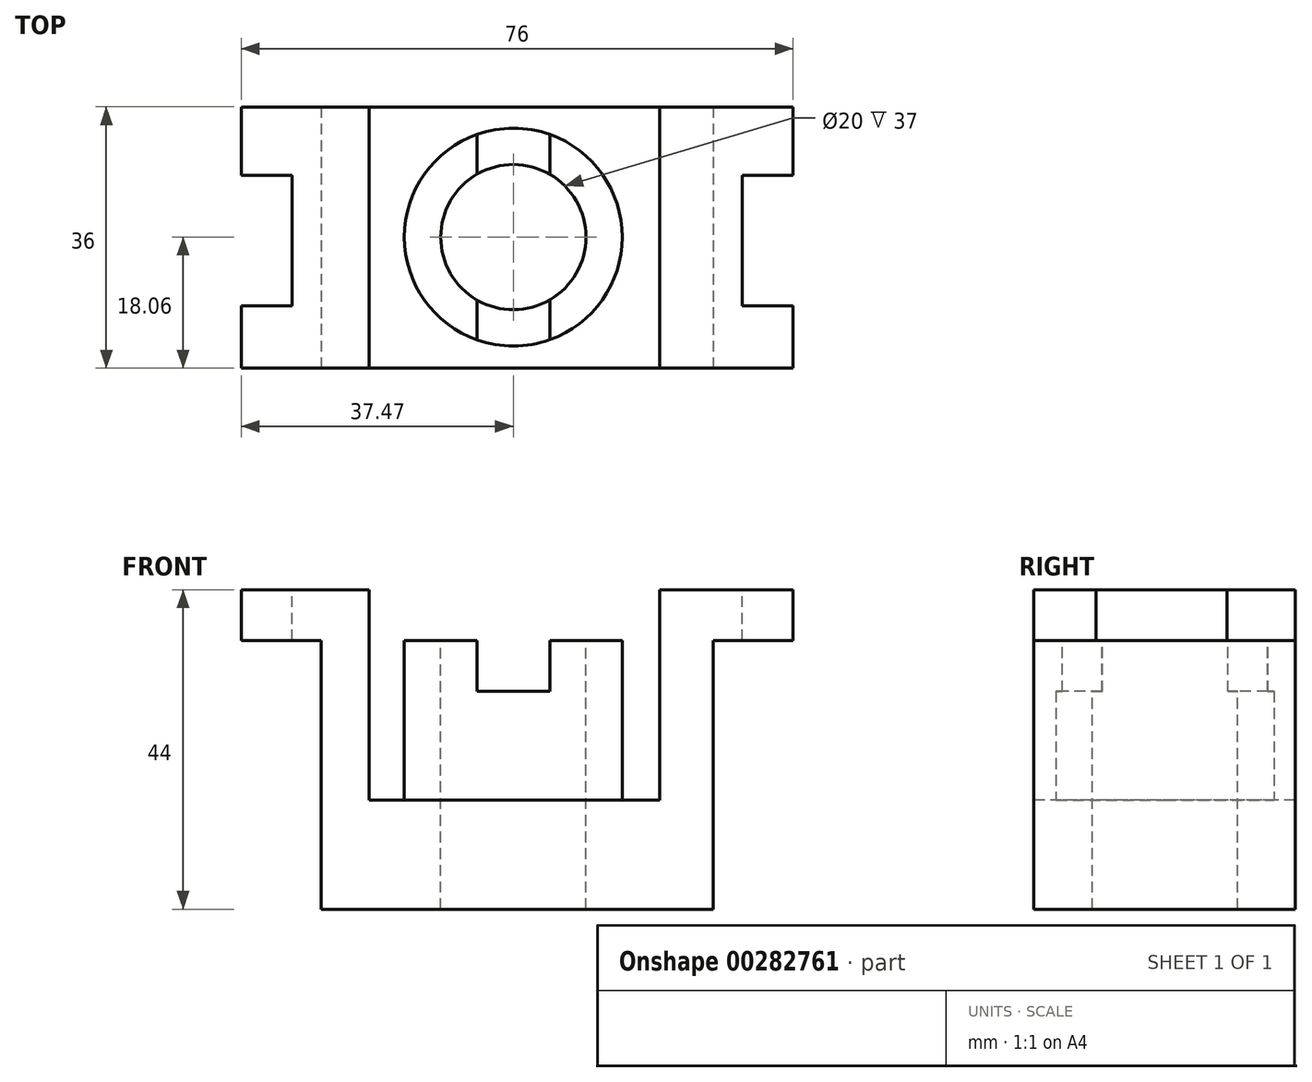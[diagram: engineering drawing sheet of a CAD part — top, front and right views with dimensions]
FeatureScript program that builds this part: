
annotation { "Feature Type Name" : "Feature", "Feature Type Description" : "" }
export const myFeature = defineFeature(function(context is Context, id is Id, definition is map)
    precondition{}
    {
        {
            var Q0;
            Q0=qCreatedBy(makeId("Top.planeOp"),FACE);
            var sketch = newSketch(context, id + "F0", { "sketchPlane" : qUnion([Q0])});
            skLineSegment(sketch, "E0.bottom", {"start": v(-14.48, -0.41) * mm, "end": v(39.52, -0.41) * mm});
            skLineSegment(sketch, "E0.top", {"start": v(-14.48, -36.41) * mm, "end": v(39.52, -36.41) * mm});
            skLineSegment(sketch, "E0.left", {"start": v(-14.48, -0.41) * mm, "end": v(-14.48, -36.41) * mm});
            skLineSegment(sketch, "E0.right", {"start": v(39.52, -0.41) * mm, "end": v(39.52, -36.41) * mm});
            skSolve(sketch);
        }
        {
            var Q0;
            Q0=makeQuery(id+"F0.imprint","IMPRINT",FACE,{"disambiguationData":[TD([[makeQuery(id+"F0.imprint","IMPRINT",EDGE,{"derivedFrom":sQuery(id+"F0.wireOp",EDGE,"E0.bottom")}),-1.0]])]});
            extrude(context, id + "F1", {"entities" : qUnion([Q0]), "depth" : 44 * mm});
        }
        {
            var Q0;
            Q0=makeQuery(id+"F1.opExtrude","SWEPT_FACE",FACE,{"disambiguationData":[OSD([sQuery(id+"F0.wireOp",EDGE,"E0.top")])]});
            var sketch = newSketch(context, id + "F2", { "sketchPlane" : qUnion([Q0])});
            skLineSegment(sketch, "E1.bottom", {"start": v(-7.85, 15) * mm, "end": v(32.15, 15) * mm});
            skLineSegment(sketch, "E1.top", {"start": v(-7.85, 44) * mm, "end": v(32.15, 44) * mm});
            skLineSegment(sketch, "E1.left", {"start": v(-7.85, 15) * mm, "end": v(-7.85, 44) * mm});
            skLineSegment(sketch, "E1.right", {"start": v(32.15, 15) * mm, "end": v(32.15, 44) * mm});
            skSolve(sketch);
        }
        {
            var Q0;
            Q0=makeQuery(id+"F2.imprint","IMPRINT",FACE,{"disambiguationData":[TD([[makeQuery(id+"F2.imprint","IMPRINT",EDGE,{"derivedFrom":sQuery(id+"F2.wireOp",EDGE,"E1.bottom")}),1.0]])]});
            extrude(context, id + "F3", {"entities" : qUnion([Q0]), "operationType" : NewBodyOperationType.REMOVE, "oppositeDirection" : true, "depth" : 36 * mm});
        }
        {
            var Q0;
            {var subQ0=sQuery(id+"F0.wireOp",EDGE,"E0.bottom");var subQ1=sQuery(id+"F0.wireOp",EDGE,"E0.right");var subQ2=sQuery(id+"F0.wireOp",EDGE,"E0.top");Q0=makeQuery(id+"F3.boolean.opBoolean","SPLIT",FACE,{"disambiguationData":[TD([makeQuery(id+"F1.opExtrude","SWEPT_FACE",FACE,{"disambiguationData":[OSD([subQ1])]})])],"derivedFrom":makeQuery(id+"F1.opExtrude","CAP_FACE",FACE,{"disambiguationData":[OSD([subQ0,subQ2,sQuery(id+"F0.wireOp",EDGE,"E0.left"),subQ1])],"isStart":false})});}
            var sketch = newSketch(context, id + "F4", { "sketchPlane" : qUnion([Q0])});
            skLineSegment(sketch, "E2.bottom", {"start": v(39.52, -0.41) * mm, "end": v(50.52, -0.41) * mm});
            skLineSegment(sketch, "E2.top", {"start": v(39.52, -36.41) * mm, "end": v(50.52, -36.41) * mm});
            skLineSegment(sketch, "E2.left", {"start": v(39.52, -0.41) * mm, "end": v(39.52, -36.41) * mm});
            skLineSegment(sketch, "E2.right", {"start": v(50.52, -0.41) * mm, "end": v(50.52, -36.41) * mm});
            skSolve(sketch);
        }
        {
            var Q0;
            Q0=makeQuery(id+"F4.imprint","IMPRINT",FACE,{"disambiguationData":[TD([[makeQuery(id+"F4.imprint","IMPRINT",EDGE,{"derivedFrom":sQuery(id+"F4.wireOp",EDGE,"E2.bottom")}),-1.0]])]});
            extrude(context, id + "F5", {"entities" : qUnion([Q0]), "operationType" : NewBodyOperationType.ADD, "oppositeDirection" : true, "depth" : 7 * mm});
        }
        {
            var Q0;
            {var subQ0=sQuery(id+"F0.wireOp",EDGE,"E0.bottom");var subQ1=sQuery(id+"F0.wireOp",EDGE,"E0.right");var subQ2=sQuery(id+"F0.wireOp",EDGE,"E0.top");Q0=makeQuery(id+"F5.boolean.opBoolean","MERGE",FACE,{"derivedFrom":[makeQuery(id+"F3.boolean.opBoolean","SPLIT",FACE,{"disambiguationData":[TD([makeQuery(id+"F1.opExtrude","SWEPT_FACE",FACE,{"disambiguationData":[OSD([subQ1])]})])],"derivedFrom":makeQuery(id+"F1.opExtrude","CAP_FACE",FACE,{"disambiguationData":[OSD([subQ0,subQ2,sQuery(id+"F0.wireOp",EDGE,"E0.left"),subQ1])],"isStart":false})}),makeQuery(id+"F5.opExtrude","CAP_FACE",FACE,{"disambiguationData":[OSD([sQuery(id+"F4.wireOp",EDGE,"E2.bottom"),sQuery(id+"F4.wireOp",EDGE,"E2.top"),sQuery(id+"F4.wireOp",EDGE,"E2.left"),sQuery(id+"F4.wireOp",EDGE,"E2.right")])],"isStart":true})]});}
            var sketch = newSketch(context, id + "F6", { "sketchPlane" : qUnion([Q0])});
            skLineSegment(sketch, "E3.bottom", {"start": v(43.52, -9.83) * mm, "end": v(50.52, -9.83) * mm});
            skLineSegment(sketch, "E3.top", {"start": v(43.52, -27.83) * mm, "end": v(50.52, -27.83) * mm});
            skLineSegment(sketch, "E3.left", {"start": v(43.52, -9.83) * mm, "end": v(43.52, -27.83) * mm});
            skLineSegment(sketch, "E3.right", {"start": v(50.52, -9.83) * mm, "end": v(50.52, -27.83) * mm});
            skSolve(sketch);
        }
        {
            var Q0;
            Q0=makeQuery(id+"F6.imprint","IMPRINT",FACE,{"disambiguationData":[TD([[makeQuery(id+"F6.imprint","IMPRINT",EDGE,{"derivedFrom":sQuery(id+"F6.wireOp",EDGE,"E3.bottom")}),-1.0]])]});
            extrude(context, id + "F7", {"entities" : qUnion([Q0]), "operationType" : NewBodyOperationType.REMOVE, "oppositeDirection" : true, "depth" : 7 * mm});
        }
        {
            var Q0;
            {var subQ0=sQuery(id+"F0.wireOp",EDGE,"E0.bottom");var subQ1=sQuery(id+"F0.wireOp",EDGE,"E0.top");var subQ2=sQuery(id+"F0.wireOp",EDGE,"E0.left");Q0=makeQuery(id+"F3.boolean.opBoolean","SPLIT",FACE,{"disambiguationData":[TD([makeQuery(id+"F1.opExtrude","SWEPT_FACE",FACE,{"disambiguationData":[OSD([subQ2])]})])],"derivedFrom":makeQuery(id+"F1.opExtrude","CAP_FACE",FACE,{"disambiguationData":[OSD([subQ0,subQ1,subQ2,sQuery(id+"F0.wireOp",EDGE,"E0.right")])],"isStart":false})});}
            var sketch = newSketch(context, id + "F8", { "sketchPlane" : qUnion([Q0])});
            skLineSegment(sketch, "E4.bottom", {"start": v(-25.48, -36.41) * mm, "end": v(-14.48, -36.41) * mm});
            skLineSegment(sketch, "E4.top", {"start": v(-25.48, -0.41) * mm, "end": v(-14.48, -0.41) * mm});
            skLineSegment(sketch, "E4.left", {"start": v(-25.48, -36.41) * mm, "end": v(-25.48, -0.41) * mm});
            skLineSegment(sketch, "E4.right", {"start": v(-14.48, -36.41) * mm, "end": v(-14.48, -0.41) * mm});
            skSolve(sketch);
        }
        {
            var Q0;
            Q0=makeQuery(id+"F8.imprint","IMPRINT",FACE,{"disambiguationData":[TD([[makeQuery(id+"F8.imprint","IMPRINT",EDGE,{"derivedFrom":sQuery(id+"F8.wireOp",EDGE,"E4.bottom")}),1.0]])]});
            extrude(context, id + "F9", {"entities" : qUnion([Q0]), "operationType" : NewBodyOperationType.ADD, "oppositeDirection" : true, "depth" : 7 * mm});
        }
        {
            var Q0;
            {var subQ0=sQuery(id+"F0.wireOp",EDGE,"E0.bottom");var subQ1=sQuery(id+"F0.wireOp",EDGE,"E0.top");var subQ2=sQuery(id+"F0.wireOp",EDGE,"E0.left");Q0=makeQuery(id+"F9.boolean.opBoolean","MERGE",FACE,{"derivedFrom":[makeQuery(id+"F3.boolean.opBoolean","SPLIT",FACE,{"disambiguationData":[TD([makeQuery(id+"F1.opExtrude","SWEPT_FACE",FACE,{"disambiguationData":[OSD([subQ2])]})])],"derivedFrom":makeQuery(id+"F1.opExtrude","CAP_FACE",FACE,{"disambiguationData":[OSD([subQ0,subQ1,subQ2,sQuery(id+"F0.wireOp",EDGE,"E0.right")])],"isStart":false})}),makeQuery(id+"F9.opExtrude","CAP_FACE",FACE,{"disambiguationData":[OSD([sQuery(id+"F8.wireOp",EDGE,"E4.bottom"),sQuery(id+"F8.wireOp",EDGE,"E4.top"),sQuery(id+"F8.wireOp",EDGE,"E4.left"),sQuery(id+"F8.wireOp",EDGE,"E4.right")])],"isStart":true})]});}
            var sketch = newSketch(context, id + "F10", { "sketchPlane" : qUnion([Q0])});
            skLineSegment(sketch, "E5.bottom", {"start": v(-18.48, -27.83) * mm, "end": v(-25.48, -27.83) * mm});
            skLineSegment(sketch, "E5.top", {"start": v(-18.48, -9.83) * mm, "end": v(-25.48, -9.83) * mm});
            skLineSegment(sketch, "E5.left", {"start": v(-18.48, -27.83) * mm, "end": v(-18.48, -9.83) * mm});
            skLineSegment(sketch, "E5.right", {"start": v(-25.48, -27.83) * mm, "end": v(-25.48, -9.83) * mm});
            skSolve(sketch);
        }
        {
            var Q0;
            Q0=makeQuery(id+"F10.imprint","IMPRINT",FACE,{"disambiguationData":[TD([[makeQuery(id+"F10.imprint","IMPRINT",EDGE,{"derivedFrom":sQuery(id+"F10.wireOp",EDGE,"E5.bottom")}),-1.0]])]});
            extrude(context, id + "F11", {"entities" : qUnion([Q0]), "operationType" : NewBodyOperationType.REMOVE, "oppositeDirection" : true, "depth" : 7 * mm});
        }
        {
            var Q0;
            Q0=makeQuery(id+"F3.boolean.opBoolean","COPY",FACE,{"derivedFrom":makeQuery(id+"F3.opExtrude","SWEPT_FACE",FACE,{"disambiguationData":[OSD([sQuery(id+"F2.wireOp",EDGE,"E1.bottom")])]})});
            var sketch = newSketch(context, id + "F12", { "sketchPlane" : qUnion([Q0])});
            skCircle(sketch, "E6", {"center": v(12, -18.35) * mm, "radius": 15 * mm});
            skSolve(sketch);
        }
        {
            var Q0;
            Q0=makeQuery(id+"F12.imprint","IMPRINT",FACE,{"disambiguationData":[TD([[makeQuery(id+"F12.imprint","IMPRINT",EDGE,{"derivedFrom":sQuery(id+"F12.wireOp",EDGE,"E6")}),1.0]])]});
            extrude(context, id + "F13", {"entities" : qUnion([Q0]), "operationType" : NewBodyOperationType.ADD, "depth" : 22 * mm});
        }
        {
            var Q0;
            Q0=makeQuery(id+"F13.opExtrude","CAP_FACE",FACE,{"disambiguationData":[OSD([sQuery(id+"F12.wireOp",EDGE,"E6")])],"isStart":false});
            var sketch = newSketch(context, id + "F14", { "sketchPlane" : qUnion([Q0])});
            skCircle(sketch, "E7", {"center": v(12, -18.35) * mm, "radius": 10 * mm});
            skSolve(sketch);
        }
        {
            var Q0;
            Q0=makeQuery(id+"F14.imprint","IMPRINT",FACE,{"disambiguationData":[TD([[makeQuery(id+"F14.imprint","IMPRINT",EDGE,{"derivedFrom":sQuery(id+"F14.wireOp",EDGE,"E7")}),1.0]])]});
            extrude(context, id + "F15", {"entities" : qUnion([Q0]), "operationType" : NewBodyOperationType.REMOVE, "oppositeDirection" : true, "depth" : 40 * mm});
        }
        {
            var Q0;
            Q0=makeQuery(id+"F13.opExtrude","CAP_FACE",FACE,{"disambiguationData":[OSD([sQuery(id+"F12.wireOp",EDGE,"E6")])],"isStart":false});
            var sketch = newSketch(context, id + "F16", { "sketchPlane" : qUnion([Q0])});
            skLineSegment(sketch, "E8.bottom", {"start": v(7.02, -0.12) * mm, "end": v(17.02, -0.12) * mm});
            skLineSegment(sketch, "E8.top", {"start": v(7.02, -36.12) * mm, "end": v(17.02, -36.12) * mm});
            skLineSegment(sketch, "E8.left", {"start": v(7.02, -0.12) * mm, "end": v(7.02, -36.12) * mm});
            skLineSegment(sketch, "E8.right", {"start": v(17.02, -0.12) * mm, "end": v(17.02, -36.12) * mm});
            skSolve(sketch);
        }
        {
            var Q0;
            {var subQ0=sQuery(id+"F16.wireOp",EDGE,"E8.left");var subQ1=makeQuery(id+"F13.opExtrude","CAP_EDGE",EDGE,{"disambiguationData":[OSD([sQuery(id+"F12.wireOp",EDGE,"E6")])],"isStart":false});var subQ2=makeQuery(id+"F16.imprint","INTERSECT",VERTEX,{"disambiguationData":[OD(0.0)],"derivedFrom":[subQ1,subQ0]});Q0=makeQuery(id+"F16.imprint","IMPRINT",FACE,{"disambiguationData":[TD([[makeQuery(id+"F16.imprint","IMPRINT",EDGE,{"disambiguationData":[TD([[subQ2,-1.0]])],"derivedFrom":subQ0}),1.0]])]});}
            var Q1;
            {var subQ0=sQuery(id+"F16.wireOp",EDGE,"E8.left");var subQ1=makeQuery(id+"F13.opExtrude","CAP_EDGE",EDGE,{"disambiguationData":[OSD([sQuery(id+"F12.wireOp",EDGE,"E6")])],"isStart":false});var subQ2=makeQuery(id+"F16.imprint","INTERSECT",VERTEX,{"disambiguationData":[OD(1.0)],"derivedFrom":[subQ1,subQ0]});Q1=makeQuery(id+"F16.imprint","IMPRINT",FACE,{"disambiguationData":[TD([[makeQuery(id+"F16.imprint","IMPRINT",EDGE,{"disambiguationData":[TD([[subQ2,1.0]])],"derivedFrom":subQ0}),1.0]])]});}
            extrude(context, id + "F17", {"entities" : qUnion([Q0, Q1]), "operationType" : NewBodyOperationType.REMOVE, "oppositeDirection" : true, "depth" : 7 * mm});
        }
    });
